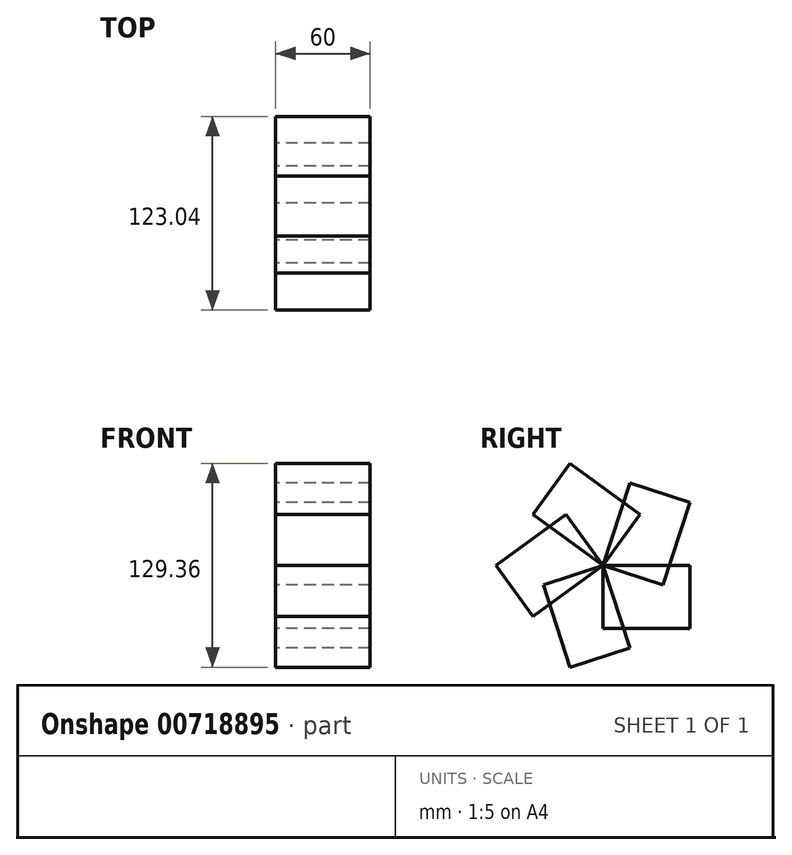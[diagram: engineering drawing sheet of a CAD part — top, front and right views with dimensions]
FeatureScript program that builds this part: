
annotation { "Feature Type Name" : "Feature", "Feature Type Description" : "" }
export const myFeature = defineFeature(function(context is Context, id is Id, definition is map)
    precondition{}
    {
        {
            var Q0;
            Q0=qCreatedBy(makeId("Top.planeOp"),FACE);
            var sketch = newSketch(context, id + "F0", { "sketchPlane" : qUnion([Q0])});
            skLineSegment(sketch, "E0.bottom", {"start": v(0, 57.19) * mm, "end": v(-60, 57.19) * mm});
            skLineSegment(sketch, "E0.top", {"start": v(0, 2.19) * mm, "end": v(-60, 2.19) * mm});
            skLineSegment(sketch, "E0.left", {"start": v(0, 57.19) * mm, "end": v(0, 2.19) * mm});
            skLineSegment(sketch, "E0.right", {"start": v(-60, 57.19) * mm, "end": v(-60, 2.19) * mm});
            skSolve(sketch);
        }
        {
            var Q0;
            Q0 = qSketchRegion(id + "F0", true);
            extrude(context, id + "F1", {"entities" : qUnion([Q0]), "depth" : 40 * mm, "offsetDistance" : 25 * mm});
        }
        {
            var Q0;
            Q0=makeQuery(id+"F1.opExtrude","SWEPT_BODY",BODY,{"disambiguationData":[OSD([sQuery(id+"F0.wireOp",EDGE,"E0.bottom"),sQuery(id+"F0.wireOp",EDGE,"E0.top"),sQuery(id+"F0.wireOp",EDGE,"E0.left"),sQuery(id+"F0.wireOp",EDGE,"E0.right")])]});
            var Q1;
            Q1=makeQuery(id+"F1.opExtrude","CAP_EDGE",EDGE,{"disambiguationData":[OSD([sQuery(id+"F0.wireOp",EDGE,"E0.top")])],"isStart":false});
            circularPattern(context, id + "F2", {"entities" : qUnion([Q0]), "axis" : qUnion([Q1]), "angle" : 360 * degree, "instanceCount" : 5, "equalSpace" : true});
        }
    });
